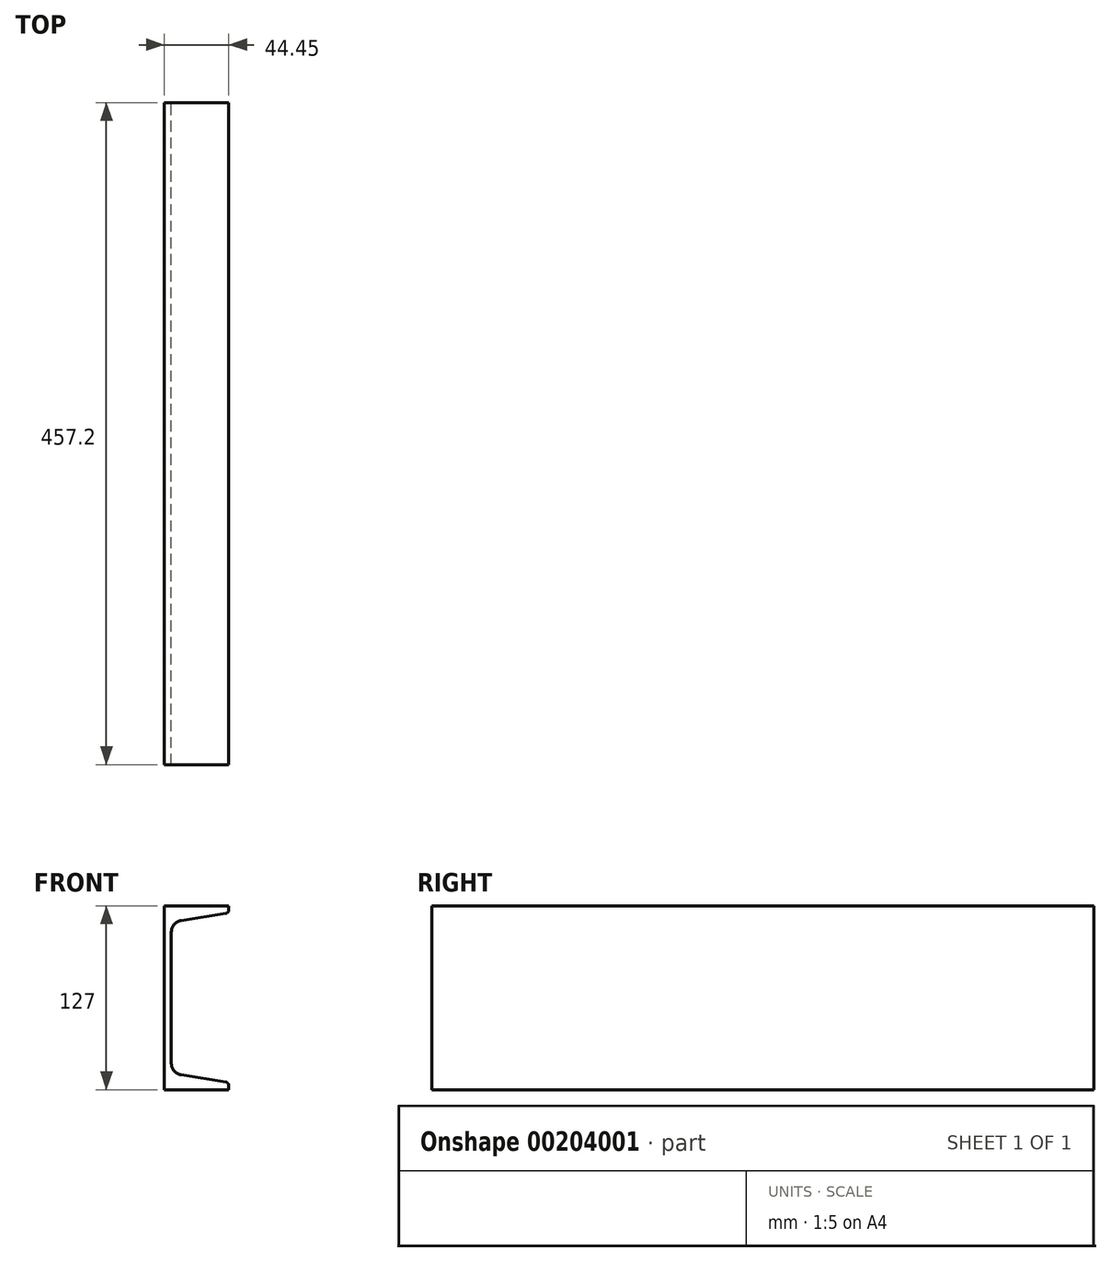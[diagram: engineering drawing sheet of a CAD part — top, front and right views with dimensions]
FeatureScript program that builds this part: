
annotation { "Feature Type Name" : "Feature", "Feature Type Description" : "" }
export const myFeature = defineFeature(function(context is Context, id is Id, definition is map)
    precondition{}
    {
        {
            var Q0;
            Q0=qCreatedBy(makeId("Front.planeOp"),FACE);
            var sketch = newSketch(context, id + "F0", { "sketchPlane" : qUnion([Q0])});
            skLineSegment(sketch, "E0", {"start": v(-601.19, 311) * mm, "end": v(-565.37, 311) * mm});
            skLineSegment(sketch, "E1", {"start": v(-567.23, 315.71) * mm, "end": v(-592.86, 319.81) * mm});
            skLineSegment(sketch, "E2", {"start": v(-601.19, 387.2) * mm, "end": v(-565.37, 387.2) * mm});
            skLineSegment(sketch, "E3", {"start": v(-567.23, 382.49) * mm, "end": v(-592.86, 378.39) * mm});
            skLineSegment(sketch, "E4", {"start": v(-596.87, 324.52) * mm, "end": v(-596.87, 373.69) * mm});
            skLineSegment(sketch, "E5", {"start": v(-601.19, 311) * mm, "end": v(-601.19, 387.2) * mm});
            skArc(sketch, "E6", {"start": v(-596.87, 324.52) * mm, "mid": v(-595.73, 321.43) * mm, "end": v(-592.86, 319.81) * mm});
            skArc(sketch, "E7", {"start": v(-592.86, 378.39) * mm, "mid": v(-595.73, 376.78) * mm, "end": v(-596.87, 373.69) * mm});
            skArc(sketch, "E8", {"start": v(-565.37, 313.53) * mm, "mid": v(-565.9, 314.97) * mm, "end": v(-567.23, 315.71) * mm});
            skArc(sketch, "E9", {"start": v(-567.23, 382.49) * mm, "mid": v(-565.9, 383.24) * mm, "end": v(-565.37, 384.67) * mm});
            skLineSegment(sketch, "E10", {"start": v(-565.37, 311) * mm, "end": v(-565.37, 313.53) * mm});
            skLineSegment(sketch, "E11", {"start": v(-565.37, 387.2) * mm, "end": v(-565.37, 384.67) * mm});
            skLineSegment(sketch, "E12", {"start": v(-606.52, 305.67) * mm, "end": v(-595.85, 316.34) * mm});
            skLineSegment(sketch, "E13", {"start": v(-606.52, 316.34) * mm, "end": v(-595.85, 305.67) * mm});
            skLineSegment(sketch, "E14", {"start": v(-458.66, 311) * mm, "end": v(-458.66, 336.4) * mm});
            skLineSegment(sketch, "E15", {"start": v(-490.16, 311) * mm, "end": v(-490.16, 336.4) * mm});
            skLineSegment(sketch, "E16", {"start": v(-494.48, 311) * mm, "end": v(-494.48, 336.4) * mm});
            skLineSegment(sketch, "E17", {"start": v(-458.66, 311) * mm, "end": v(-494.48, 311) * mm});
            skLineSegment(sketch, "E18", {"start": v(-458.66, 336.4) * mm, "end": v(-494.48, 336.4) * mm});
            skLineSegment(sketch, "E19", {"start": v(-499.81, 305.67) * mm, "end": v(-489.14, 316.34) * mm});
            skLineSegment(sketch, "E20", {"start": v(-499.81, 316.34) * mm, "end": v(-489.14, 305.67) * mm});
            skLineSegment(sketch, "E21", {"start": v(-357.16, 373.69) * mm, "end": v(-382.56, 373.69) * mm});
            skLineSegment(sketch, "E22", {"start": v(-357.16, 382.49) * mm, "end": v(-382.56, 382.49) * mm});
            skLineSegment(sketch, "E23", {"start": v(-357.16, 387.2) * mm, "end": v(-382.56, 387.2) * mm});
            skLineSegment(sketch, "E24", {"start": v(-357.16, 311) * mm, "end": v(-382.56, 311) * mm});
            skLineSegment(sketch, "E25", {"start": v(-357.16, 324.52) * mm, "end": v(-382.56, 324.52) * mm});
            skLineSegment(sketch, "E26", {"start": v(-357.16, 315.71) * mm, "end": v(-382.56, 315.71) * mm});
            skLineSegment(sketch, "E27", {"start": v(-382.56, 311) * mm, "end": v(-382.56, 387.2) * mm});
            skLineSegment(sketch, "E28", {"start": v(-357.16, 387.2) * mm, "end": v(-357.16, 311) * mm});
            skLineSegment(sketch, "E29", {"start": v(-387.9, 305.67) * mm, "end": v(-377.22, 316.34) * mm});
            skLineSegment(sketch, "E30", {"start": v(-387.9, 316.34) * mm, "end": v(-377.22, 305.67) * mm});
            skLineSegment(sketch, "E31", {"start": v(-282.07, 311) * mm, "end": v(-282.07, 387.2) * mm});
            skLineSegment(sketch, "E32", {"start": v(-244.23, 387.2) * mm, "end": v(-244.23, 384.66) * mm});
            skLineSegment(sketch, "E33", {"start": v(-246.1, 315.73) * mm, "end": v(-271.5, 319.8) * mm});
            skLineSegment(sketch, "E34", {"start": v(-282.07, 311) * mm, "end": v(-244.23, 311) * mm});
            skLineSegment(sketch, "E35", {"start": v(-246.1, 382.47) * mm, "end": v(-271.5, 378.4) * mm});
            skLineSegment(sketch, "E36", {"start": v(-275.52, 324.5) * mm, "end": v(-275.52, 373.7) * mm});
            skArc(sketch, "E37", {"start": v(-275.52, 324.5) * mm, "mid": v(-274.38, 321.4) * mm, "end": v(-271.5, 319.8) * mm});
            skArc(sketch, "E38", {"start": v(-271.5, 378.4) * mm, "mid": v(-274.38, 376.8) * mm, "end": v(-275.52, 373.7) * mm});
            skArc(sketch, "E39", {"start": v(-244.23, 313.54) * mm, "mid": v(-244.76, 314.98) * mm, "end": v(-246.1, 315.73) * mm});
            skLineSegment(sketch, "E40", {"start": v(-244.23, 311) * mm, "end": v(-244.23, 313.54) * mm});
            skArc(sketch, "E41", {"start": v(-246.1, 382.47) * mm, "mid": v(-244.76, 383.22) * mm, "end": v(-244.23, 384.66) * mm});
            skLineSegment(sketch, "E42", {"start": v(-282.07, 387.2) * mm, "end": v(-244.23, 387.2) * mm});
            skLineSegment(sketch, "E43", {"start": v(-287.4, 305.67) * mm, "end": v(-276.74, 316.34) * mm});
            skLineSegment(sketch, "E44", {"start": v(-287.4, 316.34) * mm, "end": v(-276.74, 305.67) * mm});
            skLineSegment(sketch, "E45", {"start": v(-137.41, 336.4) * mm, "end": v(-175.46, 336.4) * mm});
            skLineSegment(sketch, "E46", {"start": v(-175.46, 311) * mm, "end": v(-137.41, 311) * mm});
            skLineSegment(sketch, "E47", {"start": v(-137.41, 311) * mm, "end": v(-137.41, 336.4) * mm});
            skLineSegment(sketch, "E48", {"start": v(-175.46, 336.4) * mm, "end": v(-175.46, 311) * mm});
            skLineSegment(sketch, "E49", {"start": v(-168.9, 311) * mm, "end": v(-168.9, 336.4) * mm});
            skLineSegment(sketch, "E50", {"start": v(-180.8, 305.67) * mm, "end": v(-170.13, 316.34) * mm});
            skLineSegment(sketch, "E51", {"start": v(-180.8, 316.34) * mm, "end": v(-170.13, 305.67) * mm});
            skLineSegment(sketch, "E52", {"start": v(-62.43, 387.2) * mm, "end": v(-62.43, 311) * mm});
            skLineSegment(sketch, "E53", {"start": v(-37.03, 387.2) * mm, "end": v(-37.03, 311) * mm});
            skLineSegment(sketch, "E54", {"start": v(-37.03, 324.5) * mm, "end": v(-62.43, 324.5) * mm});
            skLineSegment(sketch, "E55", {"start": v(-37.03, 311) * mm, "end": v(-62.43, 311) * mm});
            skLineSegment(sketch, "E56", {"start": v(-37.03, 315.73) * mm, "end": v(-62.43, 315.73) * mm});
            skLineSegment(sketch, "E57", {"start": v(-37.03, 387.2) * mm, "end": v(-62.43, 387.2) * mm});
            skLineSegment(sketch, "E58", {"start": v(-37.03, 382.47) * mm, "end": v(-62.43, 382.47) * mm});
            skLineSegment(sketch, "E59", {"start": v(-37.03, 373.7) * mm, "end": v(-62.43, 373.7) * mm});
            skLineSegment(sketch, "E60", {"start": v(-67.76, 305.67) * mm, "end": v(-57.1, 316.34) * mm});
            skLineSegment(sketch, "E61", {"start": v(-67.76, 316.34) * mm, "end": v(-57.1, 305.67) * mm});
            skLineSegment(sketch, "E62", {"start": v(36.8, 311) * mm, "end": v(36.8, 387.2) * mm});
            skLineSegment(sketch, "E63", {"start": v(45.83, 324.5) * mm, "end": v(45.83, 373.7) * mm});
            skLineSegment(sketch, "E64", {"start": v(36.8, 311) * mm, "end": v(77.18, 311) * mm});
            skLineSegment(sketch, "E65", {"start": v(75.31, 315.73) * mm, "end": v(49.84, 319.8) * mm});
            skArc(sketch, "E66", {"start": v(45.83, 324.5) * mm, "mid": v(46.97, 321.41) * mm, "end": v(49.84, 319.8) * mm});
            skLineSegment(sketch, "E67", {"start": v(77.18, 311) * mm, "end": v(77.18, 313.54) * mm});
            skArc(sketch, "E68", {"start": v(77.18, 313.54) * mm, "mid": v(76.65, 314.98) * mm, "end": v(75.31, 315.73) * mm});
            skLineSegment(sketch, "E69", {"start": v(36.8, 387.2) * mm, "end": v(77.18, 387.2) * mm});
            skLineSegment(sketch, "E70", {"start": v(75.31, 382.48) * mm, "end": v(49.84, 378.4) * mm});
            skArc(sketch, "E71", {"start": v(49.84, 378.4) * mm, "mid": v(46.97, 376.79) * mm, "end": v(45.83, 373.7) * mm});
            skArc(sketch, "E72", {"start": v(75.31, 382.48) * mm, "mid": v(76.65, 383.23) * mm, "end": v(77.18, 384.66) * mm});
            skLineSegment(sketch, "E73", {"start": v(77.18, 387.2) * mm, "end": v(77.18, 384.66) * mm});
            skLineSegment(sketch, "E74", {"start": v(31.45, 305.67) * mm, "end": v(42.13, 316.34) * mm});
            skLineSegment(sketch, "E75", {"start": v(31.45, 316.34) * mm, "end": v(42.13, 305.67) * mm});
            skLineSegment(sketch, "E76", {"start": v(183.87, 311) * mm, "end": v(183.87, 336.4) * mm});
            skLineSegment(sketch, "E77", {"start": v(143.49, 311) * mm, "end": v(143.49, 336.4) * mm});
            skLineSegment(sketch, "E78", {"start": v(152.53, 311) * mm, "end": v(152.53, 336.4) * mm});
            skLineSegment(sketch, "E79", {"start": v(183.87, 311) * mm, "end": v(143.49, 311) * mm});
            skLineSegment(sketch, "E80", {"start": v(183.87, 336.4) * mm, "end": v(143.49, 336.4) * mm});
            skLineSegment(sketch, "E81", {"start": v(138.15, 305.67) * mm, "end": v(148.82, 316.34) * mm});
            skLineSegment(sketch, "E82", {"start": v(138.15, 316.34) * mm, "end": v(148.82, 305.67) * mm});
            skLineSegment(sketch, "E83", {"start": v(257.7, 387.2) * mm, "end": v(257.7, 311) * mm});
            skLineSegment(sketch, "E84", {"start": v(283.1, 387.2) * mm, "end": v(283.1, 311) * mm});
            skLineSegment(sketch, "E85", {"start": v(283.1, 324.5) * mm, "end": v(257.7, 324.5) * mm});
            skLineSegment(sketch, "E86", {"start": v(283.1, 311) * mm, "end": v(257.7, 311) * mm});
            skLineSegment(sketch, "E87", {"start": v(283.1, 315.73) * mm, "end": v(257.7, 315.73) * mm});
            skLineSegment(sketch, "E88", {"start": v(283.1, 387.2) * mm, "end": v(257.7, 387.2) * mm});
            skLineSegment(sketch, "E89", {"start": v(283.1, 382.48) * mm, "end": v(257.7, 382.48) * mm});
            skLineSegment(sketch, "E90", {"start": v(283.1, 373.7) * mm, "end": v(257.7, 373.7) * mm});
            skLineSegment(sketch, "E91", {"start": v(252.37, 305.67) * mm, "end": v(263.04, 316.34) * mm});
            skLineSegment(sketch, "E92", {"start": v(252.37, 316.34) * mm, "end": v(263.04, 305.67) * mm});
            skLineSegment(sketch, "E93", {"start": v(357, 311) * mm, "end": v(357, 412.6) * mm});
            skLineSegment(sketch, "E94", {"start": v(361.67, 326.78) * mm, "end": v(361.67, 396.82) * mm});
            skLineSegment(sketch, "E95", {"start": v(357, 311) * mm, "end": v(397.23, 311) * mm});
            skArc(sketch, "E96", {"start": v(361.67, 326.78) * mm, "mid": v(363.19, 322.66) * mm, "end": v(367.02, 320.5) * mm});
            skLineSegment(sketch, "E97", {"start": v(395.26, 315.99) * mm, "end": v(367.02, 320.5) * mm});
            skArc(sketch, "E98", {"start": v(397.23, 313.68) * mm, "mid": v(396.67, 315.2) * mm, "end": v(395.26, 315.99) * mm});
            skLineSegment(sketch, "E99", {"start": v(397.23, 311) * mm, "end": v(397.23, 313.68) * mm});
            skLineSegment(sketch, "E100", {"start": v(397.23, 412.6) * mm, "end": v(397.23, 409.92) * mm});
            skArc(sketch, "E101", {"start": v(367.02, 403.1) * mm, "mid": v(363.19, 400.94) * mm, "end": v(361.67, 396.82) * mm});
            skLineSegment(sketch, "E102", {"start": v(395.26, 407.61) * mm, "end": v(367.02, 403.1) * mm});
            skArc(sketch, "E103", {"start": v(395.26, 407.61) * mm, "mid": v(396.67, 408.4) * mm, "end": v(397.23, 409.92) * mm});
            skLineSegment(sketch, "E104", {"start": v(357, 412.6) * mm, "end": v(397.23, 412.6) * mm});
            skLineSegment(sketch, "E105", {"start": v(351.66, 305.67) * mm, "end": v(362.33, 316.34) * mm});
            skLineSegment(sketch, "E106", {"start": v(351.66, 316.34) * mm, "end": v(362.33, 305.67) * mm});
            skLineSegment(sketch, "E107", {"start": v(463.7, 336.4) * mm, "end": v(503.94, 336.4) * mm});
            skLineSegment(sketch, "E108", {"start": v(463.7, 311) * mm, "end": v(503.94, 311) * mm});
            skLineSegment(sketch, "E109", {"start": v(503.94, 311) * mm, "end": v(503.94, 336.4) * mm});
            skLineSegment(sketch, "E110", {"start": v(463.7, 311) * mm, "end": v(463.7, 336.4) * mm});
            skLineSegment(sketch, "E111", {"start": v(468.38, 311) * mm, "end": v(468.38, 336.4) * mm});
            skLineSegment(sketch, "E112", {"start": v(458.37, 305.67) * mm, "end": v(469.04, 316.34) * mm});
            skLineSegment(sketch, "E113", {"start": v(458.37, 316.34) * mm, "end": v(469.04, 305.67) * mm});
            skLineSegment(sketch, "E114", {"start": v(603.24, 412.6) * mm, "end": v(603.24, 311) * mm});
            skLineSegment(sketch, "E115", {"start": v(577.84, 412.6) * mm, "end": v(577.84, 311) * mm});
            skLineSegment(sketch, "E116", {"start": v(603.24, 311) * mm, "end": v(577.84, 311) * mm});
            skLineSegment(sketch, "E117", {"start": v(603.24, 315.99) * mm, "end": v(577.84, 315.99) * mm});
            skLineSegment(sketch, "E118", {"start": v(603.24, 326.78) * mm, "end": v(577.84, 326.78) * mm});
            skLineSegment(sketch, "E119", {"start": v(603.24, 396.82) * mm, "end": v(577.84, 396.82) * mm});
            skLineSegment(sketch, "E120", {"start": v(603.24, 407.61) * mm, "end": v(577.84, 407.61) * mm});
            skLineSegment(sketch, "E121", {"start": v(603.24, 412.6) * mm, "end": v(577.84, 412.6) * mm});
            skLineSegment(sketch, "E122", {"start": v(572.5, 305.67) * mm, "end": v(583.17, 316.34) * mm});
            skLineSegment(sketch, "E123", {"start": v(572.5, 316.34) * mm, "end": v(583.17, 305.67) * mm});
            skLineSegment(sketch, "E124", {"start": v(-596.98, 95.88) * mm, "end": v(-596.98, 165.92) * mm});
            skLineSegment(sketch, "E125", {"start": v(-605.14, 80.1) * mm, "end": v(-605.14, 181.7) * mm});
            skLineSegment(sketch, "E126", {"start": v(-563.4, 85.09) * mm, "end": v(-591.64, 89.6) * mm});
            skLineSegment(sketch, "E127", {"start": v(-605.14, 80.1) * mm, "end": v(-561.42, 80.1) * mm});
            skArc(sketch, "E128", {"start": v(-596.98, 95.88) * mm, "mid": v(-595.46, 91.76) * mm, "end": v(-591.64, 89.6) * mm});
            skArc(sketch, "E129", {"start": v(-561.42, 82.78) * mm, "mid": v(-561.98, 84.3) * mm, "end": v(-563.4, 85.09) * mm});
            skLineSegment(sketch, "E130", {"start": v(-561.42, 80.1) * mm, "end": v(-561.42, 82.78) * mm});
            skLineSegment(sketch, "E131", {"start": v(-563.4, 176.71) * mm, "end": v(-591.64, 172.2) * mm});
            skLineSegment(sketch, "E132", {"start": v(-605.14, 181.7) * mm, "end": v(-561.42, 181.7) * mm});
            skArc(sketch, "E133", {"start": v(-591.64, 172.2) * mm, "mid": v(-595.46, 170.04) * mm, "end": v(-596.98, 165.92) * mm});
            skArc(sketch, "E134", {"start": v(-563.4, 176.71) * mm, "mid": v(-561.98, 177.5) * mm, "end": v(-561.42, 179.02) * mm});
            skLineSegment(sketch, "E135", {"start": v(-561.42, 181.7) * mm, "end": v(-561.42, 179.02) * mm});
            skLineSegment(sketch, "E136", {"start": v(-610.47, 74.77) * mm, "end": v(-599.8, 85.44) * mm});
            skLineSegment(sketch, "E137", {"start": v(-610.47, 85.44) * mm, "end": v(-599.8, 74.77) * mm});
            skLineSegment(sketch, "E138", {"start": v(-454.73, 80.1) * mm, "end": v(-454.73, 105.5) * mm});
            skLineSegment(sketch, "E139", {"start": v(-498.44, 80.1) * mm, "end": v(-498.44, 105.5) * mm});
            skLineSegment(sketch, "E140", {"start": v(-490.29, 80.1) * mm, "end": v(-490.29, 105.5) * mm});
            skLineSegment(sketch, "E141", {"start": v(-454.73, 105.5) * mm, "end": v(-498.44, 105.5) * mm});
            skLineSegment(sketch, "E142", {"start": v(-454.73, 80.1) * mm, "end": v(-498.44, 80.1) * mm});
            skLineSegment(sketch, "E143", {"start": v(-503.77, 74.77) * mm, "end": v(-493.1, 85.44) * mm});
            skLineSegment(sketch, "E144", {"start": v(-503.77, 85.44) * mm, "end": v(-493.1, 74.77) * mm});
            skLineSegment(sketch, "E145", {"start": v(-357.16, 80.1) * mm, "end": v(-382.56, 80.1) * mm});
            skLineSegment(sketch, "E146", {"start": v(-357.16, 85.09) * mm, "end": v(-382.56, 85.09) * mm});
            skLineSegment(sketch, "E147", {"start": v(-357.16, 95.88) * mm, "end": v(-382.56, 95.88) * mm});
            skLineSegment(sketch, "E148", {"start": v(-357.16, 165.92) * mm, "end": v(-382.56, 165.92) * mm});
            skLineSegment(sketch, "E149", {"start": v(-357.16, 176.71) * mm, "end": v(-382.56, 176.71) * mm});
            skLineSegment(sketch, "E150", {"start": v(-357.16, 181.7) * mm, "end": v(-382.56, 181.7) * mm});
            skLineSegment(sketch, "E151", {"start": v(-382.56, 181.7) * mm, "end": v(-382.56, 80.1) * mm});
            skLineSegment(sketch, "E152", {"start": v(-357.16, 181.7) * mm, "end": v(-357.16, 80.1) * mm});
            skLineSegment(sketch, "E153", {"start": v(-387.9, 74.77) * mm, "end": v(-377.22, 85.44) * mm});
            skLineSegment(sketch, "E154", {"start": v(-387.9, 85.44) * mm, "end": v(-377.22, 74.77) * mm});
            skLineSegment(sketch, "E155", {"start": v(-285.37, 80.1) * mm, "end": v(-240.92, 80.1) * mm});
            skLineSegment(sketch, "E156", {"start": v(-285.37, 207.1) * mm, "end": v(-240.92, 207.1) * mm});
            skLineSegment(sketch, "E157", {"start": v(-243.01, 85.4) * mm, "end": v(-273.86, 90.33) * mm});
            skLineSegment(sketch, "E158", {"start": v(-243.01, 201.8) * mm, "end": v(-273.86, 196.87) * mm});
            skLineSegment(sketch, "E159", {"start": v(-285.37, 80.1) * mm, "end": v(-285.37, 207.1) * mm});
            skArc(sketch, "E160", {"start": v(-280.55, 98.17) * mm, "mid": v(-278.65, 93.02) * mm, "end": v(-273.86, 90.33) * mm});
            skArc(sketch, "E161", {"start": v(-273.86, 196.87) * mm, "mid": v(-278.65, 194.19) * mm, "end": v(-280.55, 189.04) * mm});
            skLineSegment(sketch, "E162", {"start": v(-280.55, 98.17) * mm, "end": v(-280.55, 189.04) * mm});
            skArc(sketch, "E163", {"start": v(-240.92, 82.95) * mm, "mid": v(-241.52, 84.55) * mm, "end": v(-243.01, 85.4) * mm});
            skLineSegment(sketch, "E164", {"start": v(-240.92, 80.1) * mm, "end": v(-240.92, 82.95) * mm});
            skArc(sketch, "E165", {"start": v(-243.01, 201.8) * mm, "mid": v(-241.52, 202.65) * mm, "end": v(-240.92, 204.26) * mm});
            skLineSegment(sketch, "E166", {"start": v(-240.92, 207.1) * mm, "end": v(-240.92, 204.26) * mm});
            skLineSegment(sketch, "E167", {"start": v(-290.7, 74.77) * mm, "end": v(-280.04, 85.44) * mm});
            skLineSegment(sketch, "E168", {"start": v(-290.7, 85.44) * mm, "end": v(-280.04, 74.77) * mm});
            skLineSegment(sketch, "E169", {"start": v(-134.21, 80.1) * mm, "end": v(-134.21, 105.5) * mm});
            skLineSegment(sketch, "E170", {"start": v(-178.66, 80.1) * mm, "end": v(-178.66, 105.5) * mm});
            skLineSegment(sketch, "E171", {"start": v(-173.84, 80.1) * mm, "end": v(-173.84, 105.5) * mm});
            skLineSegment(sketch, "E172", {"start": v(-134.21, 105.5) * mm, "end": v(-178.66, 105.5) * mm});
            skLineSegment(sketch, "E173", {"start": v(-134.21, 80.1) * mm, "end": v(-178.66, 80.1) * mm});
            skLineSegment(sketch, "E174", {"start": v(-184, 74.77) * mm, "end": v(-173.33, 85.44) * mm});
            skLineSegment(sketch, "E175", {"start": v(-184, 85.44) * mm, "end": v(-173.33, 74.77) * mm});
            skLineSegment(sketch, "E176", {"start": v(-37.03, 80.1) * mm, "end": v(-37.03, 207.1) * mm});
            skLineSegment(sketch, "E177", {"start": v(-62.43, 80.1) * mm, "end": v(-62.43, 207.1) * mm});
            skLineSegment(sketch, "E178", {"start": v(-37.03, 80.1) * mm, "end": v(-62.43, 80.1) * mm});
            skLineSegment(sketch, "E179", {"start": v(-37.03, 85.4) * mm, "end": v(-62.43, 85.4) * mm});
            skLineSegment(sketch, "E180", {"start": v(-37.03, 98.17) * mm, "end": v(-62.43, 98.17) * mm});
            skLineSegment(sketch, "E181", {"start": v(-37.03, 207.1) * mm, "end": v(-62.43, 207.1) * mm});
            skLineSegment(sketch, "E182", {"start": v(-37.03, 201.8) * mm, "end": v(-62.43, 201.8) * mm});
            skLineSegment(sketch, "E183", {"start": v(-37.03, 189.04) * mm, "end": v(-62.43, 189.04) * mm});
            skLineSegment(sketch, "E184", {"start": v(-67.76, 74.77) * mm, "end": v(-57.1, 85.44) * mm});
            skLineSegment(sketch, "E185", {"start": v(-67.76, 85.44) * mm, "end": v(-57.1, 74.77) * mm});
            skLineSegment(sketch, "E186", {"start": v(41.3, 98.17) * mm, "end": v(41.3, 189.04) * mm});
            skLineSegment(sketch, "E187", {"start": v(33.04, 80.1) * mm, "end": v(33.04, 207.1) * mm});
            skLineSegment(sketch, "E188", {"start": v(78.84, 85.4) * mm, "end": v(47.98, 90.33) * mm});
            skLineSegment(sketch, "E189", {"start": v(33.04, 80.1) * mm, "end": v(80.92, 80.1) * mm});
            skArc(sketch, "E190", {"start": v(41.3, 98.17) * mm, "mid": v(43.2, 93.02) * mm, "end": v(47.98, 90.33) * mm});
            skArc(sketch, "E191", {"start": v(80.92, 82.95) * mm, "mid": v(80.33, 84.55) * mm, "end": v(78.84, 85.4) * mm});
            skLineSegment(sketch, "E192", {"start": v(80.92, 80.1) * mm, "end": v(80.92, 82.95) * mm});
            skLineSegment(sketch, "E193", {"start": v(78.84, 201.8) * mm, "end": v(47.98, 196.87) * mm});
            skLineSegment(sketch, "E194", {"start": v(33.04, 207.1) * mm, "end": v(80.92, 207.1) * mm});
            skArc(sketch, "E195", {"start": v(47.98, 196.87) * mm, "mid": v(43.2, 194.19) * mm, "end": v(41.3, 189.04) * mm});
            skLineSegment(sketch, "E196", {"start": v(80.92, 207.1) * mm, "end": v(80.92, 204.26) * mm});
            skArc(sketch, "E197", {"start": v(78.84, 201.8) * mm, "mid": v(80.33, 202.65) * mm, "end": v(80.92, 204.26) * mm});
            skLineSegment(sketch, "E198", {"start": v(27.7, 74.77) * mm, "end": v(38.38, 85.44) * mm});
            skLineSegment(sketch, "E199", {"start": v(27.7, 85.44) * mm, "end": v(38.38, 74.77) * mm});
            skLineSegment(sketch, "E200", {"start": v(187.62, 80.1) * mm, "end": v(187.62, 105.5) * mm});
            skLineSegment(sketch, "E201", {"start": v(148, 80.1) * mm, "end": v(148, 105.5) * mm});
            skLineSegment(sketch, "E202", {"start": v(139.74, 105.5) * mm, "end": v(139.74, 80.1) * mm});
            skLineSegment(sketch, "E203", {"start": v(139.74, 80.1) * mm, "end": v(187.62, 80.1) * mm});
            skLineSegment(sketch, "E204", {"start": v(187.62, 105.5) * mm, "end": v(139.74, 105.5) * mm});
            skLineSegment(sketch, "E205", {"start": v(134.4, 74.77) * mm, "end": v(145.08, 85.44) * mm});
            skLineSegment(sketch, "E206", {"start": v(134.4, 85.44) * mm, "end": v(145.08, 74.77) * mm});
            skLineSegment(sketch, "E207", {"start": v(257.7, 80.1) * mm, "end": v(283.1, 80.1) * mm});
            skLineSegment(sketch, "E208", {"start": v(283.1, 207.1) * mm, "end": v(257.7, 207.1) * mm});
            skLineSegment(sketch, "E209", {"start": v(257.7, 88.03) * mm, "end": v(283.1, 88.03) * mm});
            skLineSegment(sketch, "E210", {"start": v(257.7, 199.18) * mm, "end": v(283.1, 199.18) * mm});
            skLineSegment(sketch, "E211", {"start": v(257.7, 99.15) * mm, "end": v(283.1, 99.15) * mm});
            skLineSegment(sketch, "E212", {"start": v(257.7, 188.05) * mm, "end": v(283.1, 188.05) * mm});
            skLineSegment(sketch, "E213", {"start": v(257.7, 207.1) * mm, "end": v(257.7, 80.1) * mm});
            skLineSegment(sketch, "E214", {"start": v(283.1, 80.1) * mm, "end": v(283.1, 207.1) * mm});
            skLineSegment(sketch, "E215", {"start": v(252.37, 74.77) * mm, "end": v(263.04, 85.44) * mm});
            skLineSegment(sketch, "E216", {"start": v(252.37, 85.44) * mm, "end": v(263.04, 74.77) * mm});
            skLineSegment(sketch, "E217", {"start": v(357.81, 100.43) * mm, "end": v(357.81, 212.17) * mm});
            skLineSegment(sketch, "E218", {"start": v(352.73, 80.1) * mm, "end": v(352.73, 232.5) * mm});
            skLineSegment(sketch, "E219", {"start": v(352.73, 80.1) * mm, "end": v(401.5, 80.1) * mm});
            skArc(sketch, "E220", {"start": v(357.81, 100.43) * mm, "mid": v(360.09, 94.25) * mm, "end": v(365.83, 91.03) * mm});
            skLineSegment(sketch, "E221", {"start": v(399.3, 85.67) * mm, "end": v(365.83, 91.03) * mm});
            skArc(sketch, "E222", {"start": v(401.5, 83.1) * mm, "mid": v(400.87, 84.79) * mm, "end": v(399.3, 85.67) * mm});
            skLineSegment(sketch, "E223", {"start": v(401.5, 80.1) * mm, "end": v(401.5, 83.1) * mm});
            skLineSegment(sketch, "E224", {"start": v(352.73, 232.5) * mm, "end": v(401.5, 232.5) * mm});
            skArc(sketch, "E225", {"start": v(365.83, 221.58) * mm, "mid": v(360.09, 218.35) * mm, "end": v(357.81, 212.17) * mm});
            skLineSegment(sketch, "E226", {"start": v(399.3, 226.93) * mm, "end": v(365.83, 221.58) * mm});
            skArc(sketch, "E227", {"start": v(399.3, 226.93) * mm, "mid": v(400.87, 227.82) * mm, "end": v(401.5, 229.5) * mm});
            skLineSegment(sketch, "E228", {"start": v(401.5, 232.5) * mm, "end": v(401.5, 229.5) * mm});
            skLineSegment(sketch, "E229", {"start": v(347.4, 74.77) * mm, "end": v(358.07, 85.44) * mm});
            skLineSegment(sketch, "E230", {"start": v(347.4, 85.44) * mm, "end": v(358.07, 74.77) * mm});
            skLineSegment(sketch, "E231", {"start": v(508.2, 80.1) * mm, "end": v(508.2, 105.5) * mm});
            skLineSegment(sketch, "E232", {"start": v(459.44, 105.5) * mm, "end": v(459.44, 80.1) * mm});
            skLineSegment(sketch, "E233", {"start": v(464.52, 80.1) * mm, "end": v(464.52, 105.5) * mm});
            skLineSegment(sketch, "E234", {"start": v(459.44, 80.1) * mm, "end": v(508.2, 80.1) * mm});
            skLineSegment(sketch, "E235", {"start": v(508.2, 105.5) * mm, "end": v(459.44, 105.5) * mm});
            skLineSegment(sketch, "E236", {"start": v(454.1, 74.77) * mm, "end": v(464.78, 85.44) * mm});
            skLineSegment(sketch, "E237", {"start": v(454.1, 85.44) * mm, "end": v(464.78, 74.77) * mm});
            skLineSegment(sketch, "E238", {"start": v(577.84, 232.5) * mm, "end": v(577.84, 80.1) * mm});
            skLineSegment(sketch, "E239", {"start": v(603.24, 80.1) * mm, "end": v(603.24, 232.5) * mm});
            skLineSegment(sketch, "E240", {"start": v(577.84, 80.1) * mm, "end": v(603.24, 80.1) * mm});
            skLineSegment(sketch, "E241", {"start": v(577.84, 88.03) * mm, "end": v(603.24, 88.03) * mm});
            skLineSegment(sketch, "E242", {"start": v(577.84, 100.73) * mm, "end": v(603.24, 100.73) * mm});
            skLineSegment(sketch, "E243", {"start": v(603.24, 232.5) * mm, "end": v(577.84, 232.5) * mm});
            skLineSegment(sketch, "E244", {"start": v(577.84, 224.58) * mm, "end": v(603.24, 224.58) * mm});
            skLineSegment(sketch, "E245", {"start": v(577.84, 211.88) * mm, "end": v(603.24, 211.88) * mm});
            skLineSegment(sketch, "E246", {"start": v(572.5, 74.77) * mm, "end": v(583.17, 85.44) * mm});
            skLineSegment(sketch, "E247", {"start": v(572.5, 85.44) * mm, "end": v(583.17, 74.77) * mm});
            skLineSegment(sketch, "E248", {"start": v(-609.11, -150.8) * mm, "end": v(-609.11, 1.6) * mm});
            skLineSegment(sketch, "E249", {"start": v(-601.14, -130.47) * mm, "end": v(-601.14, -18.73) * mm});
            skLineSegment(sketch, "E250", {"start": v(-559.64, -145.23) * mm, "end": v(-593.12, -139.87) * mm});
            skLineSegment(sketch, "E251", {"start": v(-609.11, -150.8) * mm, "end": v(-557.45, -150.8) * mm});
            skArc(sketch, "E252", {"start": v(-601.14, -130.47) * mm, "mid": v(-598.86, -136.65) * mm, "end": v(-593.12, -139.87) * mm});
            skArc(sketch, "E253", {"start": v(-557.45, -147.8) * mm, "mid": v(-558.07, -146.11) * mm, "end": v(-559.64, -145.23) * mm});
            skLineSegment(sketch, "E254", {"start": v(-557.45, -150.8) * mm, "end": v(-557.45, -147.8) * mm});
            skArc(sketch, "E255", {"start": v(-593.12, -9.32) * mm, "mid": v(-598.86, -12.55) * mm, "end": v(-601.14, -18.73) * mm});
            skLineSegment(sketch, "E256", {"start": v(-559.64, -3.97) * mm, "end": v(-593.12, -9.32) * mm});
            skLineSegment(sketch, "E257", {"start": v(-609.11, 1.6) * mm, "end": v(-557.45, 1.6) * mm});
            skLineSegment(sketch, "E258", {"start": v(-557.45, 1.6) * mm, "end": v(-557.45, -1.4) * mm});
            skArc(sketch, "E259", {"start": v(-559.64, -3.97) * mm, "mid": v(-558.07, -3.08) * mm, "end": v(-557.45, -1.4) * mm});
            skLineSegment(sketch, "E260", {"start": v(-614.45, -156.13) * mm, "end": v(-603.78, -145.46) * mm});
            skLineSegment(sketch, "E261", {"start": v(-614.45, -145.46) * mm, "end": v(-603.78, -156.13) * mm});
            skLineSegment(sketch, "E262", {"start": v(-449.19, -150.8) * mm, "end": v(-449.19, -125.4) * mm});
            skLineSegment(sketch, "E263", {"start": v(-503.98, -125.4) * mm, "end": v(-503.98, -150.8) * mm});
            skLineSegment(sketch, "E264", {"start": v(-496, -150.8) * mm, "end": v(-496, -125.4) * mm});
            skLineSegment(sketch, "E265", {"start": v(-449.19, -125.4) * mm, "end": v(-503.98, -125.4) * mm});
            skLineSegment(sketch, "E266", {"start": v(-503.98, -150.8) * mm, "end": v(-449.19, -150.8) * mm});
            skLineSegment(sketch, "E267", {"start": v(-509.31, -156.13) * mm, "end": v(-498.64, -145.46) * mm});
            skLineSegment(sketch, "E268", {"start": v(-509.31, -145.46) * mm, "end": v(-498.64, -156.13) * mm});
            skLineSegment(sketch, "E269", {"start": v(-357.16, -150.8) * mm, "end": v(-357.16, 1.6) * mm});
            skLineSegment(sketch, "E270", {"start": v(-382.56, -130.17) * mm, "end": v(-357.16, -130.17) * mm});
            skLineSegment(sketch, "E271", {"start": v(-382.56, -142.87) * mm, "end": v(-357.16, -142.87) * mm});
            skLineSegment(sketch, "E272", {"start": v(-382.56, -150.8) * mm, "end": v(-357.16, -150.8) * mm});
            skLineSegment(sketch, "E273", {"start": v(-382.56, -19.02) * mm, "end": v(-357.16, -19.02) * mm});
            skLineSegment(sketch, "E274", {"start": v(-382.56, -6.32) * mm, "end": v(-357.16, -6.32) * mm});
            skLineSegment(sketch, "E275", {"start": v(-357.16, 1.6) * mm, "end": v(-382.56, 1.6) * mm});
            skLineSegment(sketch, "E276", {"start": v(-382.56, 1.6) * mm, "end": v(-382.56, -150.8) * mm});
            skLineSegment(sketch, "E277", {"start": v(-387.9, -156.13) * mm, "end": v(-377.22, -145.46) * mm});
            skLineSegment(sketch, "E278", {"start": v(-387.9, -145.46) * mm, "end": v(-377.22, -156.13) * mm});
            skLineSegment(sketch, "E279", {"start": v(-294.86, -150.8) * mm, "end": v(-294.86, 1.6) * mm});
            skLineSegment(sketch, "E280", {"start": v(-286.99, -128.7) * mm, "end": v(-286.99, -20.49) * mm});
            skLineSegment(sketch, "E281", {"start": v(-294.86, -150.8) * mm, "end": v(-231.44, -150.8) * mm});
            skLineSegment(sketch, "E282", {"start": v(-233.58, -145.37) * mm, "end": v(-278.97, -138.11) * mm});
            skArc(sketch, "E283", {"start": v(-286.99, -128.7) * mm, "mid": v(-284.7, -134.89) * mm, "end": v(-278.97, -138.11) * mm});
            skLineSegment(sketch, "E284", {"start": v(-231.44, -150.8) * mm, "end": v(-231.44, -147.88) * mm});
            skArc(sketch, "E285", {"start": v(-231.44, -147.88) * mm, "mid": v(-232.04, -146.24) * mm, "end": v(-233.58, -145.37) * mm});
            skArc(sketch, "E286", {"start": v(-278.97, -11.08) * mm, "mid": v(-284.7, -14.3) * mm, "end": v(-286.99, -20.49) * mm});
            skLineSegment(sketch, "E287", {"start": v(-233.58, -3.82) * mm, "end": v(-278.97, -11.08) * mm});
            skLineSegment(sketch, "E288", {"start": v(-294.86, 1.6) * mm, "end": v(-231.44, 1.6) * mm});
            skLineSegment(sketch, "E289", {"start": v(-231.44, 1.6) * mm, "end": v(-231.44, -1.31) * mm});
            skArc(sketch, "E290", {"start": v(-233.58, -3.82) * mm, "mid": v(-232.04, -2.96) * mm, "end": v(-231.44, -1.31) * mm});
            skLineSegment(sketch, "E291", {"start": v(-300.2, -156.13) * mm, "end": v(-289.52, -145.46) * mm});
            skLineSegment(sketch, "E292", {"start": v(-300.2, -145.46) * mm, "end": v(-289.52, -156.13) * mm});
            skLineSegment(sketch, "E293", {"start": v(-124.73, -150.8) * mm, "end": v(-124.73, -125.4) * mm});
            skLineSegment(sketch, "E294", {"start": v(-188.15, -125.4) * mm, "end": v(-188.15, -150.8) * mm});
            skLineSegment(sketch, "E295", {"start": v(-180.28, -150.8) * mm, "end": v(-180.28, -125.4) * mm});
            skLineSegment(sketch, "E296", {"start": v(-124.73, -125.4) * mm, "end": v(-188.15, -125.4) * mm});
            skLineSegment(sketch, "E297", {"start": v(-188.15, -150.8) * mm, "end": v(-124.73, -150.8) * mm});
            skLineSegment(sketch, "E298", {"start": v(-193.49, -156.13) * mm, "end": v(-182.81, -145.46) * mm});
            skLineSegment(sketch, "E299", {"start": v(-193.49, -145.46) * mm, "end": v(-182.81, -156.13) * mm});
            skLineSegment(sketch, "E300", {"start": v(-62.43, -19.02) * mm, "end": v(-37.03, -19.02) * mm});
            skLineSegment(sketch, "E301", {"start": v(-62.43, -130.17) * mm, "end": v(-37.03, -130.17) * mm});
            skLineSegment(sketch, "E302", {"start": v(-62.43, -7.92) * mm, "end": v(-37.03, -7.92) * mm});
            skLineSegment(sketch, "E303", {"start": v(-62.43, -141.27) * mm, "end": v(-37.03, -141.27) * mm});
            skLineSegment(sketch, "E304", {"start": v(-37.03, 1.6) * mm, "end": v(-62.43, 1.6) * mm});
            skLineSegment(sketch, "E305", {"start": v(-62.43, -150.8) * mm, "end": v(-37.03, -150.8) * mm});
            skLineSegment(sketch, "E306", {"start": v(-37.03, -150.8) * mm, "end": v(-37.03, 1.6) * mm});
            skLineSegment(sketch, "E307", {"start": v(-62.43, 1.6) * mm, "end": v(-62.43, -150.8) * mm});
            skLineSegment(sketch, "E308", {"start": v(-67.76, -156.13) * mm, "end": v(-57.1, -145.46) * mm});
            skLineSegment(sketch, "E309", {"start": v(-67.76, -145.46) * mm, "end": v(-57.1, -156.13) * mm});
            skLineSegment(sketch, "E310", {"start": v(29.59, -150.8) * mm, "end": v(29.59, 1.6) * mm});
            skLineSegment(sketch, "E311", {"start": v(40.69, -130.47) * mm, "end": v(40.69, -18.73) * mm});
            skArc(sketch, "E312", {"start": v(84.38, -147.8) * mm, "mid": v(83.75, -146.11) * mm, "end": v(82.18, -145.23) * mm});
            skLineSegment(sketch, "E313", {"start": v(82.18, -145.23) * mm, "end": v(48.7, -139.87) * mm});
            skLineSegment(sketch, "E314", {"start": v(29.59, -150.8) * mm, "end": v(84.38, -150.8) * mm});
            skLineSegment(sketch, "E315", {"start": v(84.38, -150.8) * mm, "end": v(84.38, -147.8) * mm});
            skArc(sketch, "E316", {"start": v(40.69, -130.47) * mm, "mid": v(42.97, -136.65) * mm, "end": v(48.7, -139.87) * mm});
            skArc(sketch, "E317", {"start": v(82.18, -3.97) * mm, "mid": v(83.75, -3.08) * mm, "end": v(84.38, -1.4) * mm});
            skLineSegment(sketch, "E318", {"start": v(82.18, -3.97) * mm, "end": v(48.7, -9.32) * mm});
            skArc(sketch, "E319", {"start": v(48.7, -9.32) * mm, "mid": v(42.97, -12.55) * mm, "end": v(40.69, -18.73) * mm});
            skLineSegment(sketch, "E320", {"start": v(29.59, 1.6) * mm, "end": v(84.38, 1.6) * mm});
            skLineSegment(sketch, "E321", {"start": v(84.38, 1.6) * mm, "end": v(84.38, -1.4) * mm});
            skLineSegment(sketch, "E322", {"start": v(24.25, -156.13) * mm, "end": v(34.92, -145.46) * mm});
            skLineSegment(sketch, "E323", {"start": v(24.25, -145.46) * mm, "end": v(34.92, -156.13) * mm});
            skLineSegment(sketch, "E324", {"start": v(151, -130.17) * mm, "end": v(176.4, -130.17) * mm});
            skLineSegment(sketch, "E325", {"start": v(151, -142.87) * mm, "end": v(176.4, -142.87) * mm});
            skLineSegment(sketch, "E326", {"start": v(151, -150.8) * mm, "end": v(176.4, -150.8) * mm});
            skLineSegment(sketch, "E327", {"start": v(151, -19.02) * mm, "end": v(176.4, -19.02) * mm});
            skLineSegment(sketch, "E328", {"start": v(151, -6.32) * mm, "end": v(176.4, -6.32) * mm});
            skLineSegment(sketch, "E329", {"start": v(176.4, 1.6) * mm, "end": v(151, 1.6) * mm});
            skLineSegment(sketch, "E330", {"start": v(151, 1.6) * mm, "end": v(151, -150.8) * mm});
            skLineSegment(sketch, "E331", {"start": v(176.4, -150.8) * mm, "end": v(176.4, 1.6) * mm});
            skLineSegment(sketch, "E332", {"start": v(145.66, -156.13) * mm, "end": v(156.33, -145.46) * mm});
            skLineSegment(sketch, "E333", {"start": v(145.66, -145.46) * mm, "end": v(156.33, -156.13) * mm});
            skLineSegment(sketch, "E334", {"start": v(297.79, -150.8) * mm, "end": v(297.79, -125.4) * mm});
            skLineSegment(sketch, "E335", {"start": v(243, -125.4) * mm, "end": v(243, -150.8) * mm});
            skLineSegment(sketch, "E336", {"start": v(254.1, -150.8) * mm, "end": v(254.1, -125.4) * mm});
            skLineSegment(sketch, "E337", {"start": v(297.79, -125.4) * mm, "end": v(243, -125.4) * mm});
            skLineSegment(sketch, "E338", {"start": v(243, -150.8) * mm, "end": v(297.79, -150.8) * mm});
            skLineSegment(sketch, "E339", {"start": v(237.66, -156.13) * mm, "end": v(248.33, -145.46) * mm});
            skLineSegment(sketch, "E340", {"start": v(237.66, -145.46) * mm, "end": v(248.33, -156.13) * mm});
            skLineSegment(sketch, "E341", {"start": v(339.76, -150.8) * mm, "end": v(339.76, 1.6) * mm});
            skLineSegment(sketch, "E342", {"start": v(347.8, -125.28) * mm, "end": v(347.8, -23.92) * mm});
            skLineSegment(sketch, "E343", {"start": v(339.76, -150.8) * mm, "end": v(414.47, -150.8) * mm});
            skLineSegment(sketch, "E344", {"start": v(411.63, -143.61) * mm, "end": v(355.81, -134.68) * mm});
            skArc(sketch, "E345", {"start": v(347.8, -125.28) * mm, "mid": v(350.07, -131.46) * mm, "end": v(355.81, -134.68) * mm});
            skArc(sketch, "E346", {"start": v(414.47, -146.94) * mm, "mid": v(413.66, -144.75) * mm, "end": v(411.63, -143.61) * mm});
            skLineSegment(sketch, "E347", {"start": v(414.47, -150.8) * mm, "end": v(414.47, -146.94) * mm});
            skLineSegment(sketch, "E348", {"start": v(411.63, -5.58) * mm, "end": v(355.81, -14.51) * mm});
            skArc(sketch, "E349", {"start": v(355.81, -14.51) * mm, "mid": v(350.07, -17.74) * mm, "end": v(347.8, -23.92) * mm});
            skLineSegment(sketch, "E350", {"start": v(339.76, 1.6) * mm, "end": v(414.47, 1.6) * mm});
            skArc(sketch, "E351", {"start": v(411.63, -5.58) * mm, "mid": v(413.66, -4.44) * mm, "end": v(414.47, -2.26) * mm});
            skLineSegment(sketch, "E352", {"start": v(414.47, 1.6) * mm, "end": v(414.47, -2.26) * mm});
            skLineSegment(sketch, "E353", {"start": v(334.43, -156.13) * mm, "end": v(345.1, -145.46) * mm});
            skLineSegment(sketch, "E354", {"start": v(334.43, -145.46) * mm, "end": v(345.1, -156.13) * mm});
            skLineSegment(sketch, "E355", {"start": v(521.18, -125.4) * mm, "end": v(446.47, -125.4) * mm});
            skLineSegment(sketch, "E356", {"start": v(446.47, -150.8) * mm, "end": v(521.18, -150.8) * mm});
            skLineSegment(sketch, "E357", {"start": v(454.5, -150.8) * mm, "end": v(454.5, -125.4) * mm});
            skLineSegment(sketch, "E358", {"start": v(446.47, -125.4) * mm, "end": v(446.47, -150.8) * mm});
            skLineSegment(sketch, "E359", {"start": v(521.18, -150.8) * mm, "end": v(521.18, -125.4) * mm});
            skLineSegment(sketch, "E360", {"start": v(441.14, -156.13) * mm, "end": v(451.8, -145.46) * mm});
            skLineSegment(sketch, "E361", {"start": v(441.14, -145.46) * mm, "end": v(451.8, -156.13) * mm});
            skLineSegment(sketch, "E362", {"start": v(577.84, -150.8) * mm, "end": v(603.24, -150.8) * mm});
            skLineSegment(sketch, "E363", {"start": v(603.24, 1.6) * mm, "end": v(577.84, 1.6) * mm});
            skLineSegment(sketch, "E364", {"start": v(577.84, -138.1) * mm, "end": v(603.24, -138.1) * mm});
            skLineSegment(sketch, "E365", {"start": v(577.84, -11.1) * mm, "end": v(603.24, -11.1) * mm});
            skLineSegment(sketch, "E366", {"start": v(577.84, -123.82) * mm, "end": v(603.24, -123.82) * mm});
            skLineSegment(sketch, "E367", {"start": v(577.84, -25.37) * mm, "end": v(603.24, -25.37) * mm});
            skLineSegment(sketch, "E368", {"start": v(603.24, -150.8) * mm, "end": v(603.24, 1.6) * mm});
            skLineSegment(sketch, "E369", {"start": v(577.84, 1.6) * mm, "end": v(577.84, -150.8) * mm});
            skLineSegment(sketch, "E370", {"start": v(572.5, -156.13) * mm, "end": v(583.17, -145.46) * mm});
            skLineSegment(sketch, "E371", {"start": v(572.5, -145.46) * mm, "end": v(583.17, -156.13) * mm});
            skLineSegment(sketch, "E372", {"start": v(-621.38, -381.7) * mm, "end": v(-621.38, -229.3) * mm});
            skLineSegment(sketch, "E373", {"start": v(-611.85, -356.18) * mm, "end": v(-611.85, -254.82) * mm});
            skLineSegment(sketch, "E374", {"start": v(-548.01, -374.51) * mm, "end": v(-603.83, -365.58) * mm});
            skArc(sketch, "E375", {"start": v(-611.85, -356.18) * mm, "mid": v(-609.58, -362.36) * mm, "end": v(-603.83, -365.58) * mm});
            skLineSegment(sketch, "E376", {"start": v(-621.38, -381.7) * mm, "end": v(-545.18, -381.7) * mm});
            skArc(sketch, "E377", {"start": v(-545.18, -377.84) * mm, "mid": v(-545.98, -375.65) * mm, "end": v(-548.01, -374.51) * mm});
            skLineSegment(sketch, "E378", {"start": v(-545.18, -381.7) * mm, "end": v(-545.18, -377.84) * mm});
            skLineSegment(sketch, "E379", {"start": v(-548.01, -236.48) * mm, "end": v(-603.83, -245.41) * mm});
            skLineSegment(sketch, "E380", {"start": v(-621.38, -229.3) * mm, "end": v(-545.18, -229.3) * mm});
            skArc(sketch, "E381", {"start": v(-603.83, -245.41) * mm, "mid": v(-609.58, -248.64) * mm, "end": v(-611.85, -254.82) * mm});
            skLineSegment(sketch, "E382", {"start": v(-545.18, -229.3) * mm, "end": v(-545.18, -233.16) * mm});
            skArc(sketch, "E383", {"start": v(-548.01, -236.48) * mm, "mid": v(-545.98, -235.34) * mm, "end": v(-545.18, -233.16) * mm});
            skLineSegment(sketch, "E384", {"start": v(-626.72, -387.03) * mm, "end": v(-616.04, -376.36) * mm});
            skLineSegment(sketch, "E385", {"start": v(-626.72, -376.36) * mm, "end": v(-616.04, -387.03) * mm});
            skLineSegment(sketch, "E386", {"start": v(-432.13, -381.7) * mm, "end": v(-432.13, -356.3) * mm});
            skLineSegment(sketch, "E387", {"start": v(-521.03, -356.3) * mm, "end": v(-521.03, -381.7) * mm});
            skLineSegment(sketch, "E388", {"start": v(-512.4, -381.7) * mm, "end": v(-512.4, -356.3) * mm});
            skLineSegment(sketch, "E389", {"start": v(-432.13, -356.3) * mm, "end": v(-521.03, -356.3) * mm});
            skLineSegment(sketch, "E390", {"start": v(-521.03, -381.7) * mm, "end": v(-432.13, -381.7) * mm});
            skLineSegment(sketch, "E391", {"start": v(-526.37, -387.03) * mm, "end": v(-515.7, -376.36) * mm});
            skLineSegment(sketch, "E392", {"start": v(-526.37, -376.36) * mm, "end": v(-515.7, -387.03) * mm});
            skLineSegment(sketch, "E393", {"start": v(-382.56, -256.27) * mm, "end": v(-357.16, -256.27) * mm});
            skLineSegment(sketch, "E394", {"start": v(-382.56, -354.72) * mm, "end": v(-357.16, -354.72) * mm});
            skLineSegment(sketch, "E395", {"start": v(-382.56, -235.65) * mm, "end": v(-357.16, -235.65) * mm});
            skLineSegment(sketch, "E396", {"start": v(-382.56, -375.35) * mm, "end": v(-357.16, -375.35) * mm});
            skLineSegment(sketch, "E397", {"start": v(-357.16, -229.3) * mm, "end": v(-382.56, -229.3) * mm});
            skLineSegment(sketch, "E398", {"start": v(-382.56, -381.7) * mm, "end": v(-357.16, -381.7) * mm});
            skLineSegment(sketch, "E399", {"start": v(-357.16, -381.7) * mm, "end": v(-357.16, -229.3) * mm});
            skLineSegment(sketch, "E400", {"start": v(-382.56, -229.3) * mm, "end": v(-382.56, -381.7) * mm});
            skLineSegment(sketch, "E401", {"start": v(-387.9, -387.03) * mm, "end": v(-377.22, -376.36) * mm});
            skLineSegment(sketch, "E402", {"start": v(-387.9, -376.36) * mm, "end": v(-377.22, -387.03) * mm});
            skSolve(sketch);
        }
        {
            var Q0;
            Q0 = qSketchRegion(id + "F0", true);
            extrude(context, id + "F1", {"entities" : qUnion([Q0]), "depth" : 457.2 * mm});
        }
        {
            var Q0;
            Q0=makeQuery(id+"F1.opExtrude","SWEPT_BODY",BODY,{"disambiguationData":[OSD([sQuery(id+"F0.wireOp",EDGE,"E169"),sQuery(id+"F0.wireOp",EDGE,"E170"),sQuery(id+"F0.wireOp",EDGE,"E172"),sQuery(id+"F0.wireOp",EDGE,"E173")])]});
            var Q1;
            Q1=makeQuery(id+"F1.opExtrude","SWEPT_BODY",BODY,{"disambiguationData":[OSD([sQuery(id+"F0.wireOp",EDGE,"E176"),sQuery(id+"F0.wireOp",EDGE,"E177"),sQuery(id+"F0.wireOp",EDGE,"E178"),sQuery(id+"F0.wireOp",EDGE,"E181")])]});
            var Q2;
            Q2=makeQuery(id+"F1.opExtrude","SWEPT_BODY",BODY,{"disambiguationData":[OSD([sQuery(id+"F0.wireOp",EDGE,"E186"),sQuery(id+"F0.wireOp",EDGE,"E187"),sQuery(id+"F0.wireOp",EDGE,"E188"),sQuery(id+"F0.wireOp",EDGE,"E189"),sQuery(id+"F0.wireOp",EDGE,"E190"),sQuery(id+"F0.wireOp",EDGE,"E191"),sQuery(id+"F0.wireOp",EDGE,"E192"),sQuery(id+"F0.wireOp",EDGE,"E193"),sQuery(id+"F0.wireOp",EDGE,"E194"),sQuery(id+"F0.wireOp",EDGE,"E195"),sQuery(id+"F0.wireOp",EDGE,"E196"),sQuery(id+"F0.wireOp",EDGE,"E197")])]});
            var Q3;
            Q3=makeQuery(id+"F1.opExtrude","SWEPT_BODY",BODY,{"disambiguationData":[OSD([sQuery(id+"F0.wireOp",EDGE,"E200"),sQuery(id+"F0.wireOp",EDGE,"E202"),sQuery(id+"F0.wireOp",EDGE,"E203"),sQuery(id+"F0.wireOp",EDGE,"E204")])]});
            var Q4;
            Q4=makeQuery(id+"F1.opExtrude","SWEPT_BODY",BODY,{"disambiguationData":[OSD([sQuery(id+"F0.wireOp",EDGE,"E207"),sQuery(id+"F0.wireOp",EDGE,"E208"),sQuery(id+"F0.wireOp",EDGE,"E213"),sQuery(id+"F0.wireOp",EDGE,"E214")])]});
            var Q5;
            Q5=makeQuery(id+"F1.opExtrude","SWEPT_BODY",BODY,{"disambiguationData":[OSD([sQuery(id+"F0.wireOp",EDGE,"E217"),sQuery(id+"F0.wireOp",EDGE,"E218"),sQuery(id+"F0.wireOp",EDGE,"E219"),sQuery(id+"F0.wireOp",EDGE,"E220"),sQuery(id+"F0.wireOp",EDGE,"E221"),sQuery(id+"F0.wireOp",EDGE,"E222"),sQuery(id+"F0.wireOp",EDGE,"E223"),sQuery(id+"F0.wireOp",EDGE,"E224"),sQuery(id+"F0.wireOp",EDGE,"E225"),sQuery(id+"F0.wireOp",EDGE,"E226"),sQuery(id+"F0.wireOp",EDGE,"E227"),sQuery(id+"F0.wireOp",EDGE,"E228")])]});
            var Q6;
            Q6=makeQuery(id+"F1.opExtrude","SWEPT_BODY",BODY,{"disambiguationData":[OSD([sQuery(id+"F0.wireOp",EDGE,"E231"),sQuery(id+"F0.wireOp",EDGE,"E232"),sQuery(id+"F0.wireOp",EDGE,"E234"),sQuery(id+"F0.wireOp",EDGE,"E235")])]});
            var Q7;
            Q7=makeQuery(id+"F1.opExtrude","SWEPT_BODY",BODY,{"disambiguationData":[OSD([sQuery(id+"F0.wireOp",EDGE,"E238"),sQuery(id+"F0.wireOp",EDGE,"E239"),sQuery(id+"F0.wireOp",EDGE,"E240"),sQuery(id+"F0.wireOp",EDGE,"E243")])]});
            var Q8;
            Q8=makeQuery(id+"F1.opExtrude","SWEPT_BODY",BODY,{"disambiguationData":[OSD([sQuery(id+"F0.wireOp",EDGE,"E248"),sQuery(id+"F0.wireOp",EDGE,"E249"),sQuery(id+"F0.wireOp",EDGE,"E250"),sQuery(id+"F0.wireOp",EDGE,"E251"),sQuery(id+"F0.wireOp",EDGE,"E252"),sQuery(id+"F0.wireOp",EDGE,"E253"),sQuery(id+"F0.wireOp",EDGE,"E254"),sQuery(id+"F0.wireOp",EDGE,"E255"),sQuery(id+"F0.wireOp",EDGE,"E256"),sQuery(id+"F0.wireOp",EDGE,"E257"),sQuery(id+"F0.wireOp",EDGE,"E258"),sQuery(id+"F0.wireOp",EDGE,"E259")])]});
            var Q9;
            Q9=makeQuery(id+"F1.opExtrude","SWEPT_BODY",BODY,{"disambiguationData":[OSD([sQuery(id+"F0.wireOp",EDGE,"E262"),sQuery(id+"F0.wireOp",EDGE,"E263"),sQuery(id+"F0.wireOp",EDGE,"E265"),sQuery(id+"F0.wireOp",EDGE,"E266")])]});
            var Q10;
            Q10=makeQuery(id+"F1.opExtrude","SWEPT_BODY",BODY,{"disambiguationData":[OSD([sQuery(id+"F0.wireOp",EDGE,"E269"),sQuery(id+"F0.wireOp",EDGE,"E272"),sQuery(id+"F0.wireOp",EDGE,"E275"),sQuery(id+"F0.wireOp",EDGE,"E276")])]});
            var Q11;
            Q11=makeQuery(id+"F1.opExtrude","SWEPT_BODY",BODY,{"disambiguationData":[OSD([sQuery(id+"F0.wireOp",EDGE,"E279"),sQuery(id+"F0.wireOp",EDGE,"E280"),sQuery(id+"F0.wireOp",EDGE,"E281"),sQuery(id+"F0.wireOp",EDGE,"E282"),sQuery(id+"F0.wireOp",EDGE,"E283"),sQuery(id+"F0.wireOp",EDGE,"E284"),sQuery(id+"F0.wireOp",EDGE,"E285"),sQuery(id+"F0.wireOp",EDGE,"E286"),sQuery(id+"F0.wireOp",EDGE,"E287"),sQuery(id+"F0.wireOp",EDGE,"E288"),sQuery(id+"F0.wireOp",EDGE,"E289"),sQuery(id+"F0.wireOp",EDGE,"E290")])]});
            var Q12;
            Q12=makeQuery(id+"F1.opExtrude","SWEPT_BODY",BODY,{"disambiguationData":[OSD([sQuery(id+"F0.wireOp",EDGE,"E293"),sQuery(id+"F0.wireOp",EDGE,"E294"),sQuery(id+"F0.wireOp",EDGE,"E296"),sQuery(id+"F0.wireOp",EDGE,"E297")])]});
            var Q13;
            Q13=makeQuery(id+"F1.opExtrude","SWEPT_BODY",BODY,{"disambiguationData":[OSD([sQuery(id+"F0.wireOp",EDGE,"E304"),sQuery(id+"F0.wireOp",EDGE,"E305"),sQuery(id+"F0.wireOp",EDGE,"E306"),sQuery(id+"F0.wireOp",EDGE,"E307")])]});
            var Q14;
            Q14=makeQuery(id+"F1.opExtrude","SWEPT_BODY",BODY,{"disambiguationData":[OSD([sQuery(id+"F0.wireOp",EDGE,"E310"),sQuery(id+"F0.wireOp",EDGE,"E311"),sQuery(id+"F0.wireOp",EDGE,"E312"),sQuery(id+"F0.wireOp",EDGE,"E313"),sQuery(id+"F0.wireOp",EDGE,"E314"),sQuery(id+"F0.wireOp",EDGE,"E315"),sQuery(id+"F0.wireOp",EDGE,"E316"),sQuery(id+"F0.wireOp",EDGE,"E317"),sQuery(id+"F0.wireOp",EDGE,"E318"),sQuery(id+"F0.wireOp",EDGE,"E319"),sQuery(id+"F0.wireOp",EDGE,"E320"),sQuery(id+"F0.wireOp",EDGE,"E321")])]});
            var Q15;
            Q15=makeQuery(id+"F1.opExtrude","SWEPT_BODY",BODY,{"disambiguationData":[OSD([sQuery(id+"F0.wireOp",EDGE,"E326"),sQuery(id+"F0.wireOp",EDGE,"E329"),sQuery(id+"F0.wireOp",EDGE,"E330"),sQuery(id+"F0.wireOp",EDGE,"E331")])]});
            var Q16;
            Q16=makeQuery(id+"F1.opExtrude","SWEPT_BODY",BODY,{"disambiguationData":[OSD([sQuery(id+"F0.wireOp",EDGE,"E334"),sQuery(id+"F0.wireOp",EDGE,"E335"),sQuery(id+"F0.wireOp",EDGE,"E337"),sQuery(id+"F0.wireOp",EDGE,"E338")])]});
            var Q17;
            Q17=makeQuery(id+"F1.opExtrude","SWEPT_BODY",BODY,{"disambiguationData":[OSD([sQuery(id+"F0.wireOp",EDGE,"E341"),sQuery(id+"F0.wireOp",EDGE,"E342"),sQuery(id+"F0.wireOp",EDGE,"E343"),sQuery(id+"F0.wireOp",EDGE,"E344"),sQuery(id+"F0.wireOp",EDGE,"E345"),sQuery(id+"F0.wireOp",EDGE,"E346"),sQuery(id+"F0.wireOp",EDGE,"E347"),sQuery(id+"F0.wireOp",EDGE,"E348"),sQuery(id+"F0.wireOp",EDGE,"E349"),sQuery(id+"F0.wireOp",EDGE,"E350"),sQuery(id+"F0.wireOp",EDGE,"E351"),sQuery(id+"F0.wireOp",EDGE,"E352")])]});
            var Q18;
            Q18=makeQuery(id+"F1.opExtrude","SWEPT_BODY",BODY,{"disambiguationData":[OSD([sQuery(id+"F0.wireOp",EDGE,"E355"),sQuery(id+"F0.wireOp",EDGE,"E356"),sQuery(id+"F0.wireOp",EDGE,"E358"),sQuery(id+"F0.wireOp",EDGE,"E359")])]});
            var Q19;
            Q19=makeQuery(id+"F1.opExtrude","SWEPT_BODY",BODY,{"disambiguationData":[OSD([sQuery(id+"F0.wireOp",EDGE,"E362"),sQuery(id+"F0.wireOp",EDGE,"E363"),sQuery(id+"F0.wireOp",EDGE,"E368"),sQuery(id+"F0.wireOp",EDGE,"E369")])]});
            var Q20;
            Q20=makeQuery(id+"F1.opExtrude","SWEPT_BODY",BODY,{"disambiguationData":[OSD([sQuery(id+"F0.wireOp",EDGE,"E372"),sQuery(id+"F0.wireOp",EDGE,"E373"),sQuery(id+"F0.wireOp",EDGE,"E374"),sQuery(id+"F0.wireOp",EDGE,"E375"),sQuery(id+"F0.wireOp",EDGE,"E376"),sQuery(id+"F0.wireOp",EDGE,"E377"),sQuery(id+"F0.wireOp",EDGE,"E378"),sQuery(id+"F0.wireOp",EDGE,"E379"),sQuery(id+"F0.wireOp",EDGE,"E380"),sQuery(id+"F0.wireOp",EDGE,"E381"),sQuery(id+"F0.wireOp",EDGE,"E382"),sQuery(id+"F0.wireOp",EDGE,"E383")])]});
            var Q21;
            Q21=makeQuery(id+"F1.opExtrude","SWEPT_BODY",BODY,{"disambiguationData":[OSD([sQuery(id+"F0.wireOp",EDGE,"E386"),sQuery(id+"F0.wireOp",EDGE,"E387"),sQuery(id+"F0.wireOp",EDGE,"E389"),sQuery(id+"F0.wireOp",EDGE,"E390")])]});
            var Q22;
            Q22=makeQuery(id+"F1.opExtrude","SWEPT_BODY",BODY,{"disambiguationData":[OSD([sQuery(id+"F0.wireOp",EDGE,"E397"),sQuery(id+"F0.wireOp",EDGE,"E398"),sQuery(id+"F0.wireOp",EDGE,"E399"),sQuery(id+"F0.wireOp",EDGE,"E400")])]});
            var Q23;
            Q23=makeQuery(id+"F1.opExtrude","SWEPT_BODY",BODY,{"disambiguationData":[OSD([sQuery(id+"F0.wireOp",EDGE,"E0"),sQuery(id+"F0.wireOp",EDGE,"E1"),sQuery(id+"F0.wireOp",EDGE,"E2"),sQuery(id+"F0.wireOp",EDGE,"E3"),sQuery(id+"F0.wireOp",EDGE,"E4"),sQuery(id+"F0.wireOp",EDGE,"E5"),sQuery(id+"F0.wireOp",EDGE,"E6"),sQuery(id+"F0.wireOp",EDGE,"E7"),sQuery(id+"F0.wireOp",EDGE,"E8"),sQuery(id+"F0.wireOp",EDGE,"E9"),sQuery(id+"F0.wireOp",EDGE,"E10"),sQuery(id+"F0.wireOp",EDGE,"E11")])]});
            var Q24;
            Q24=makeQuery(id+"F1.opExtrude","SWEPT_BODY",BODY,{"disambiguationData":[OSD([sQuery(id+"F0.wireOp",EDGE,"E14"),sQuery(id+"F0.wireOp",EDGE,"E16"),sQuery(id+"F0.wireOp",EDGE,"E17"),sQuery(id+"F0.wireOp",EDGE,"E18")])]});
            var Q25;
            Q25=makeQuery(id+"F1.opExtrude","SWEPT_BODY",BODY,{"disambiguationData":[OSD([sQuery(id+"F0.wireOp",EDGE,"E23"),sQuery(id+"F0.wireOp",EDGE,"E24"),sQuery(id+"F0.wireOp",EDGE,"E27"),sQuery(id+"F0.wireOp",EDGE,"E28")])]});
            var Q26;
            Q26=makeQuery(id+"F1.opExtrude","SWEPT_BODY",BODY,{"disambiguationData":[OSD([sQuery(id+"F0.wireOp",EDGE,"E45"),sQuery(id+"F0.wireOp",EDGE,"E46"),sQuery(id+"F0.wireOp",EDGE,"E47"),sQuery(id+"F0.wireOp",EDGE,"E48")])]});
            var Q27;
            Q27=makeQuery(id+"F1.opExtrude","SWEPT_BODY",BODY,{"disambiguationData":[OSD([sQuery(id+"F0.wireOp",EDGE,"E62"),sQuery(id+"F0.wireOp",EDGE,"E63"),sQuery(id+"F0.wireOp",EDGE,"E64"),sQuery(id+"F0.wireOp",EDGE,"E65"),sQuery(id+"F0.wireOp",EDGE,"E66"),sQuery(id+"F0.wireOp",EDGE,"E67"),sQuery(id+"F0.wireOp",EDGE,"E68"),sQuery(id+"F0.wireOp",EDGE,"E69"),sQuery(id+"F0.wireOp",EDGE,"E70"),sQuery(id+"F0.wireOp",EDGE,"E71"),sQuery(id+"F0.wireOp",EDGE,"E72"),sQuery(id+"F0.wireOp",EDGE,"E73")])]});
            var Q28;
            Q28=makeQuery(id+"F1.opExtrude","SWEPT_BODY",BODY,{"disambiguationData":[OSD([sQuery(id+"F0.wireOp",EDGE,"E83"),sQuery(id+"F0.wireOp",EDGE,"E84"),sQuery(id+"F0.wireOp",EDGE,"E86"),sQuery(id+"F0.wireOp",EDGE,"E88")])]});
            var Q29;
            Q29=makeQuery(id+"F1.opExtrude","SWEPT_BODY",BODY,{"disambiguationData":[OSD([sQuery(id+"F0.wireOp",EDGE,"E31"),sQuery(id+"F0.wireOp",EDGE,"E32"),sQuery(id+"F0.wireOp",EDGE,"E33"),sQuery(id+"F0.wireOp",EDGE,"E34"),sQuery(id+"F0.wireOp",EDGE,"E35"),sQuery(id+"F0.wireOp",EDGE,"E36"),sQuery(id+"F0.wireOp",EDGE,"E37"),sQuery(id+"F0.wireOp",EDGE,"E38"),sQuery(id+"F0.wireOp",EDGE,"E39"),sQuery(id+"F0.wireOp",EDGE,"E40"),sQuery(id+"F0.wireOp",EDGE,"E41"),sQuery(id+"F0.wireOp",EDGE,"E42")])]});
            var Q30;
            Q30=makeQuery(id+"F1.opExtrude","SWEPT_BODY",BODY,{"disambiguationData":[OSD([sQuery(id+"F0.wireOp",EDGE,"E52"),sQuery(id+"F0.wireOp",EDGE,"E53"),sQuery(id+"F0.wireOp",EDGE,"E55"),sQuery(id+"F0.wireOp",EDGE,"E57")])]});
            var Q31;
            Q31=makeQuery(id+"F1.opExtrude","SWEPT_BODY",BODY,{"disambiguationData":[OSD([sQuery(id+"F0.wireOp",EDGE,"E76"),sQuery(id+"F0.wireOp",EDGE,"E77"),sQuery(id+"F0.wireOp",EDGE,"E79"),sQuery(id+"F0.wireOp",EDGE,"E80")])]});
            var Q32;
            Q32=makeQuery(id+"F1.opExtrude","SWEPT_BODY",BODY,{"disambiguationData":[OSD([sQuery(id+"F0.wireOp",EDGE,"E93"),sQuery(id+"F0.wireOp",EDGE,"E94"),sQuery(id+"F0.wireOp",EDGE,"E95"),sQuery(id+"F0.wireOp",EDGE,"E96"),sQuery(id+"F0.wireOp",EDGE,"E97"),sQuery(id+"F0.wireOp",EDGE,"E98"),sQuery(id+"F0.wireOp",EDGE,"E99"),sQuery(id+"F0.wireOp",EDGE,"E100"),sQuery(id+"F0.wireOp",EDGE,"E101"),sQuery(id+"F0.wireOp",EDGE,"E102"),sQuery(id+"F0.wireOp",EDGE,"E103"),sQuery(id+"F0.wireOp",EDGE,"E104")])]});
            var Q33;
            Q33=makeQuery(id+"F1.opExtrude","SWEPT_BODY",BODY,{"disambiguationData":[OSD([sQuery(id+"F0.wireOp",EDGE,"E107"),sQuery(id+"F0.wireOp",EDGE,"E108"),sQuery(id+"F0.wireOp",EDGE,"E109"),sQuery(id+"F0.wireOp",EDGE,"E110")])]});
            var Q34;
            Q34=makeQuery(id+"F1.opExtrude","SWEPT_BODY",BODY,{"disambiguationData":[OSD([sQuery(id+"F0.wireOp",EDGE,"E114"),sQuery(id+"F0.wireOp",EDGE,"E115"),sQuery(id+"F0.wireOp",EDGE,"E116"),sQuery(id+"F0.wireOp",EDGE,"E121")])]});
            var Q35;
            Q35=makeQuery(id+"F1.opExtrude","SWEPT_BODY",BODY,{"disambiguationData":[OSD([sQuery(id+"F0.wireOp",EDGE,"E124"),sQuery(id+"F0.wireOp",EDGE,"E125"),sQuery(id+"F0.wireOp",EDGE,"E126"),sQuery(id+"F0.wireOp",EDGE,"E127"),sQuery(id+"F0.wireOp",EDGE,"E128"),sQuery(id+"F0.wireOp",EDGE,"E129"),sQuery(id+"F0.wireOp",EDGE,"E130"),sQuery(id+"F0.wireOp",EDGE,"E131"),sQuery(id+"F0.wireOp",EDGE,"E132"),sQuery(id+"F0.wireOp",EDGE,"E133"),sQuery(id+"F0.wireOp",EDGE,"E134"),sQuery(id+"F0.wireOp",EDGE,"E135")])]});
            var Q36;
            Q36=makeQuery(id+"F1.opExtrude","SWEPT_BODY",BODY,{"disambiguationData":[OSD([sQuery(id+"F0.wireOp",EDGE,"E138"),sQuery(id+"F0.wireOp",EDGE,"E139"),sQuery(id+"F0.wireOp",EDGE,"E141"),sQuery(id+"F0.wireOp",EDGE,"E142")])]});
            var Q37;
            Q37=makeQuery(id+"F1.opExtrude","SWEPT_BODY",BODY,{"disambiguationData":[OSD([sQuery(id+"F0.wireOp",EDGE,"E145"),sQuery(id+"F0.wireOp",EDGE,"E150"),sQuery(id+"F0.wireOp",EDGE,"E151"),sQuery(id+"F0.wireOp",EDGE,"E152")])]});
            deleteBodies(context, id + "F2", {"entities" : qUnion([Q0, Q1, Q2, Q3, Q4, Q5, Q6, Q7, Q8, Q9, Q10, Q11, Q12, Q13, Q14, Q15, Q16, Q17, Q18, Q19, Q20, Q21, Q22, Q23, Q24, Q25, Q26, Q27, Q28, Q29, Q30, Q31, Q32, Q33, Q34, Q35, Q36, Q37])});
        }
    });
